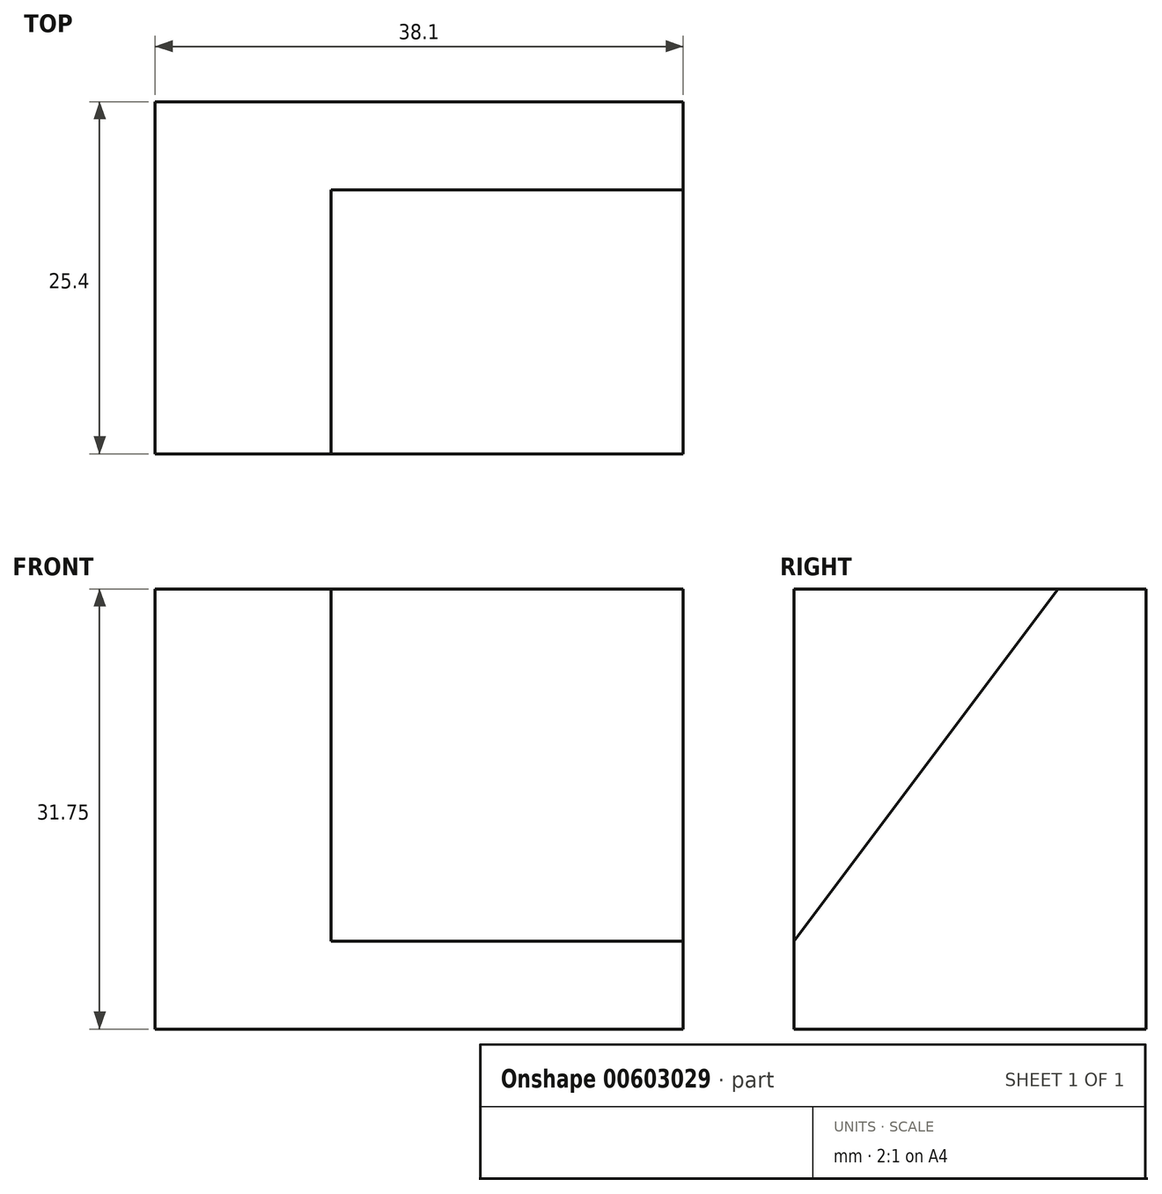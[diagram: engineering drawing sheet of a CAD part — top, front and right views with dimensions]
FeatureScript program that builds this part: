
annotation { "Feature Type Name" : "Feature", "Feature Type Description" : "" }
export const myFeature = defineFeature(function(context is Context, id is Id, definition is map)
    precondition{}
    {
        {
            var Q0;
            Q0=qCreatedBy(makeId("Front.planeOp"),FACE);
            var sketch = newSketch(context, id + "F0", { "sketchPlane" : qUnion([Q0])});
            skLineSegment(sketch, "E0", {"start": v(0, 0) * mm, "end": v(0, 31.75) * mm});
            skLineSegment(sketch, "E1", {"start": v(0, 31.75) * mm, "end": v(38.1, 31.75) * mm});
            skLineSegment(sketch, "E2", {"start": v(38.1, 31.75) * mm, "end": v(38.1, 0) * mm});
            skLineSegment(sketch, "E3", {"start": v(38.1, 0) * mm, "end": v(0, 0) * mm});
            skSolve(sketch);
        }
        {
            var Q0;
            Q0 = qSketchRegion(id + "F0", true);
            extrude(context, id + "F1", {"entities" : qUnion([Q0]), "depth" : 25.4 * mm, "offsetDistance" : 25.4 * mm});
        }
        {
            var Q0;
            Q0=makeQuery(id+"F1.opExtrude","SWEPT_FACE",FACE,{"disambiguationData":[OSD([sQuery(id+"F0.wireOp",EDGE,"E2")])]});
            var sketch = newSketch(context, id + "F2", { "sketchPlane" : qUnion([Q0])});
            skLineSegment(sketch, "E4", {"start": v(0, 31.75) * mm, "end": v(-6.35, 31.75) * mm});
            skLineSegment(sketch, "E5", {"start": v(-25.4, 0) * mm, "end": v(-25.4, 6.35) * mm});
            skLineSegment(sketch, "E6", {"start": v(-25.4, 6.35) * mm, "end": v(-6.35, 31.75) * mm});
            skLineSegment(sketch, "E7", {"start": v(-6.35, 31.75) * mm, "end": v(-25.4, 31.75) * mm});
            skLineSegment(sketch, "E8", {"start": v(-25.4, 31.75) * mm, "end": v(-25.4, 6.35) * mm});
            skSolve(sketch);
        }
        {
            var Q0;
            Q0=makeQuery(id+"F2.imprint","IMPRINT",FACE,{"disambiguationData":[TD([[makeQuery(id+"F2.imprint","IMPRINT",EDGE,{"derivedFrom":sQuery(id+"F2.wireOp",EDGE,"E6")}),1.0]])]});
            extrude(context, id + "F3", {"entities" : qUnion([Q0]), "operationType" : NewBodyOperationType.REMOVE, "oppositeDirection" : true, "depth" : 25.4 * mm, "offsetDistance" : 25.4 * mm});
        }
    });
